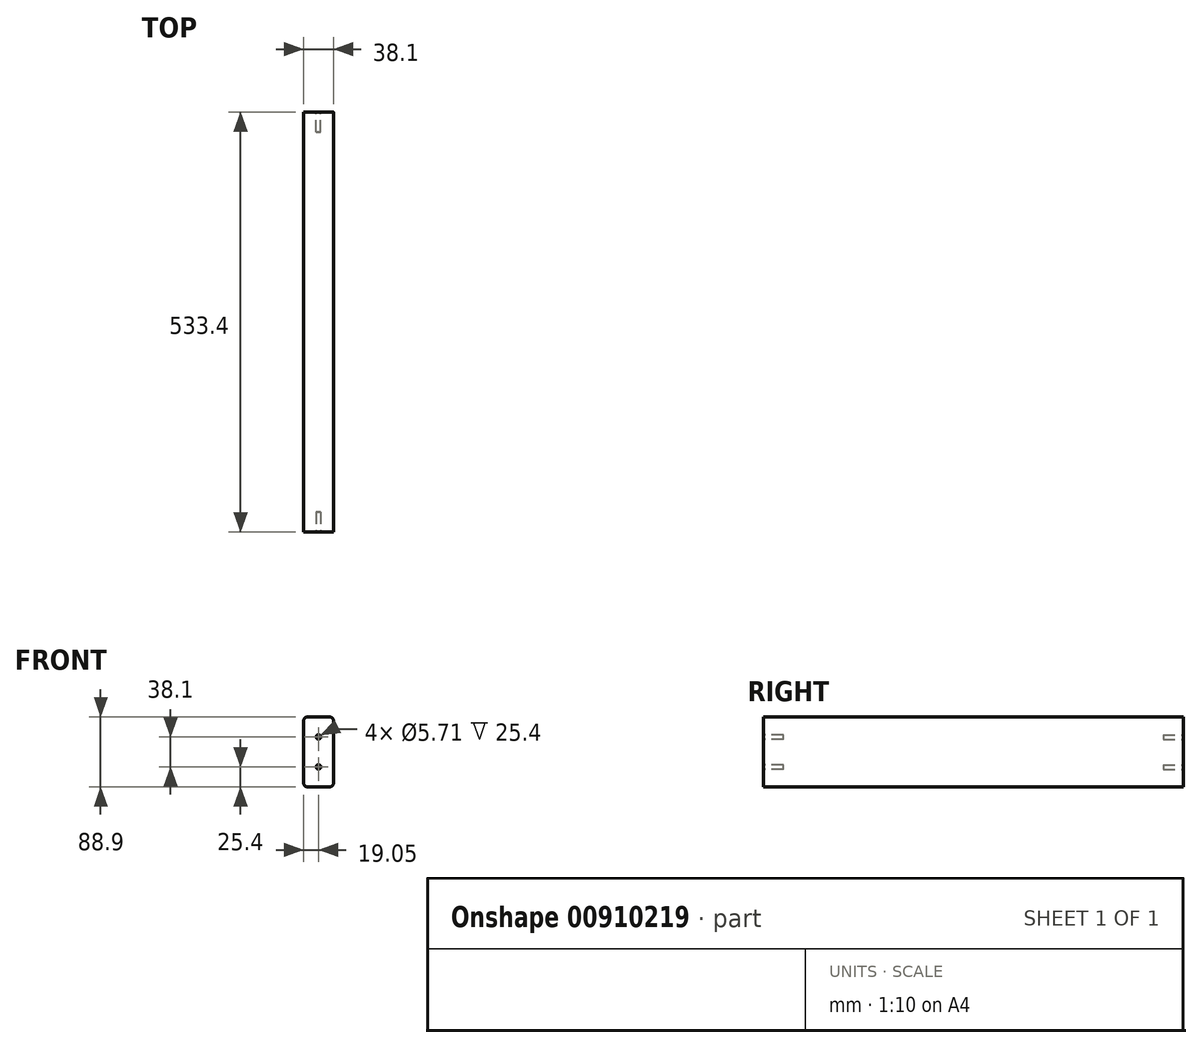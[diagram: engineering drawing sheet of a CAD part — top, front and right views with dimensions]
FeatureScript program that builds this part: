
annotation { "Feature Type Name" : "Feature", "Feature Type Description" : "" }
export const myFeature = defineFeature(function(context is Context, id is Id, definition is map)
    precondition{}
    {
        {
            var Q0;
            Q0=qCreatedBy(makeId("Front.planeOp"),FACE);
            var sketch = newSketch(context, id + "F0", { "sketchPlane" : qUnion([Q0])});
            skLineSegment(sketch, "E0.bottom", {"start": v(-19.05, 44.45) * mm, "end": v(19.05, 44.45) * mm});
            skLineSegment(sketch, "E0.top", {"start": v(-19.05, -44.45) * mm, "end": v(19.05, -44.45) * mm});
            skLineSegment(sketch, "E0.left", {"start": v(-19.05, 44.45) * mm, "end": v(-19.05, -44.45) * mm});
            skLineSegment(sketch, "E0.right", {"start": v(19.05, 44.45) * mm, "end": v(19.05, -44.45) * mm});
            skPoint(sketch, "E0.middle", {"position": v(0, 0) * mm});
            skSolve(sketch);
        }
        {
            var Q0;
            Q0 = qSketchRegion(id + "F0", true);
            extrude(context, id + "F1", {"entities" : qUnion([Q0]), "depth" : 533.4 * mm, "offsetDistance" : 25.4 * mm});
        }
        {
            var Q0;
            Q0=makeQuery(id+"F1.opExtrude","SWEPT_EDGE",EDGE,{"disambiguationData":[OSD([sQuery(id+"F0.wireOp",EDGE,"E0.bottom"),sQuery(id+"F0.wireOp",EDGE,"E0.right")])]});
            var Q1;
            Q1=makeQuery(id+"F1.opExtrude","SWEPT_EDGE",EDGE,{"disambiguationData":[OSD([sQuery(id+"F0.wireOp",EDGE,"E0.bottom"),sQuery(id+"F0.wireOp",EDGE,"E0.left")])]});
            var Q2;
            Q2=makeQuery(id+"F1.opExtrude","SWEPT_EDGE",EDGE,{"disambiguationData":[OSD([sQuery(id+"F0.wireOp",EDGE,"E0.top"),sQuery(id+"F0.wireOp",EDGE,"E0.right")])]});
            var Q3;
            Q3=makeQuery(id+"F1.opExtrude","SWEPT_EDGE",EDGE,{"disambiguationData":[OSD([sQuery(id+"F0.wireOp",EDGE,"E0.top"),sQuery(id+"F0.wireOp",EDGE,"E0.left")])]});
            fillet(context, id + "F2", {"entities" : qUnion([Q0, Q1, Q2, Q3]), "radius" : 5.08 * mm, "tangentPropagation" : true, "allowEdgeOverflow" : false});
        }
        {
            var Q0;
            Q0=makeQuery(id+"F1.opExtrude","CAP_FACE",FACE,{"disambiguationData":[OSD([sQuery(id+"F0.wireOp",EDGE,"E0.bottom"),sQuery(id+"F0.wireOp",EDGE,"E0.top"),sQuery(id+"F0.wireOp",EDGE,"E0.left"),sQuery(id+"F0.wireOp",EDGE,"E0.right")])],"isStart":false});
            var sketch = newSketch(context, id + "F3", { "sketchPlane" : qUnion([Q0])});
            skLineSegment(sketch, "E1", {"start": v(0, 44.45) * mm, "end": v(0, -44.45) * mm, "construction": true});
            skCircle(sketch, "E2", {"center": v(0, -19.05) * mm, "radius": 2.86 * mm});
            skCircle(sketch, "E3", {"center": v(0, 19.05) * mm, "radius": 2.86 * mm});
            skSolve(sketch);
        }
        {
            var Q0;
            Q0 = qSketchRegion(id + "F3", true);
            extrude(context, id + "F4", {"entities" : qUnion([Q0]), "operationType" : NewBodyOperationType.REMOVE, "oppositeDirection" : true, "depth" : 25.4 * mm, "offsetDistance" : 25.4 * mm});
        }
        {
            var Q0;
            Q0=makeQuery(id+"F1.opExtrude","CAP_FACE",FACE,{"disambiguationData":[OSD([sQuery(id+"F0.wireOp",EDGE,"E0.bottom"),sQuery(id+"F0.wireOp",EDGE,"E0.top"),sQuery(id+"F0.wireOp",EDGE,"E0.left"),sQuery(id+"F0.wireOp",EDGE,"E0.right")])],"isStart":true});
            var sketch = newSketch(context, id + "F5", { "sketchPlane" : qUnion([Q0])});
            skLineSegment(sketch, "E4", {"start": v(0, 44.45) * mm, "end": v(0, -44.45) * mm, "construction": true});
            skCircle(sketch, "E5", {"center": v(0, -19.05) * mm, "radius": 2.86 * mm});
            skCircle(sketch, "E6", {"center": v(0, 19.05) * mm, "radius": 2.86 * mm});
            skSolve(sketch);
        }
        {
            var Q0;
            Q0=makeQuery(id+"F5.imprint","IMPRINT",FACE,{"disambiguationData":[TD([[makeQuery(id+"F5.imprint","IMPRINT",EDGE,{"derivedFrom":sQuery(id+"F5.wireOp",EDGE,"E6")}),1.0]])]});
            var Q1;
            Q1=makeQuery(id+"F5.imprint","IMPRINT",FACE,{"disambiguationData":[TD([[makeQuery(id+"F5.imprint","IMPRINT",EDGE,{"derivedFrom":sQuery(id+"F5.wireOp",EDGE,"E5")}),1.0]])]});
            var Q2;
            Q2=sQuery(id+"F5.wireOp",EDGE,"E5");
            var Q3;
            Q3=sQuery(id+"F5.wireOp",EDGE,"E6");
            extrude(context, id + "F6", {"entities" : qUnion([Q0, Q1]), "operationType" : NewBodyOperationType.REMOVE, "surfaceEntities" : qUnion([Q2, Q3]), "oppositeDirection" : true, "depth" : 25.4 * mm, "offsetDistance" : 25.4 * mm});
        }
    });
